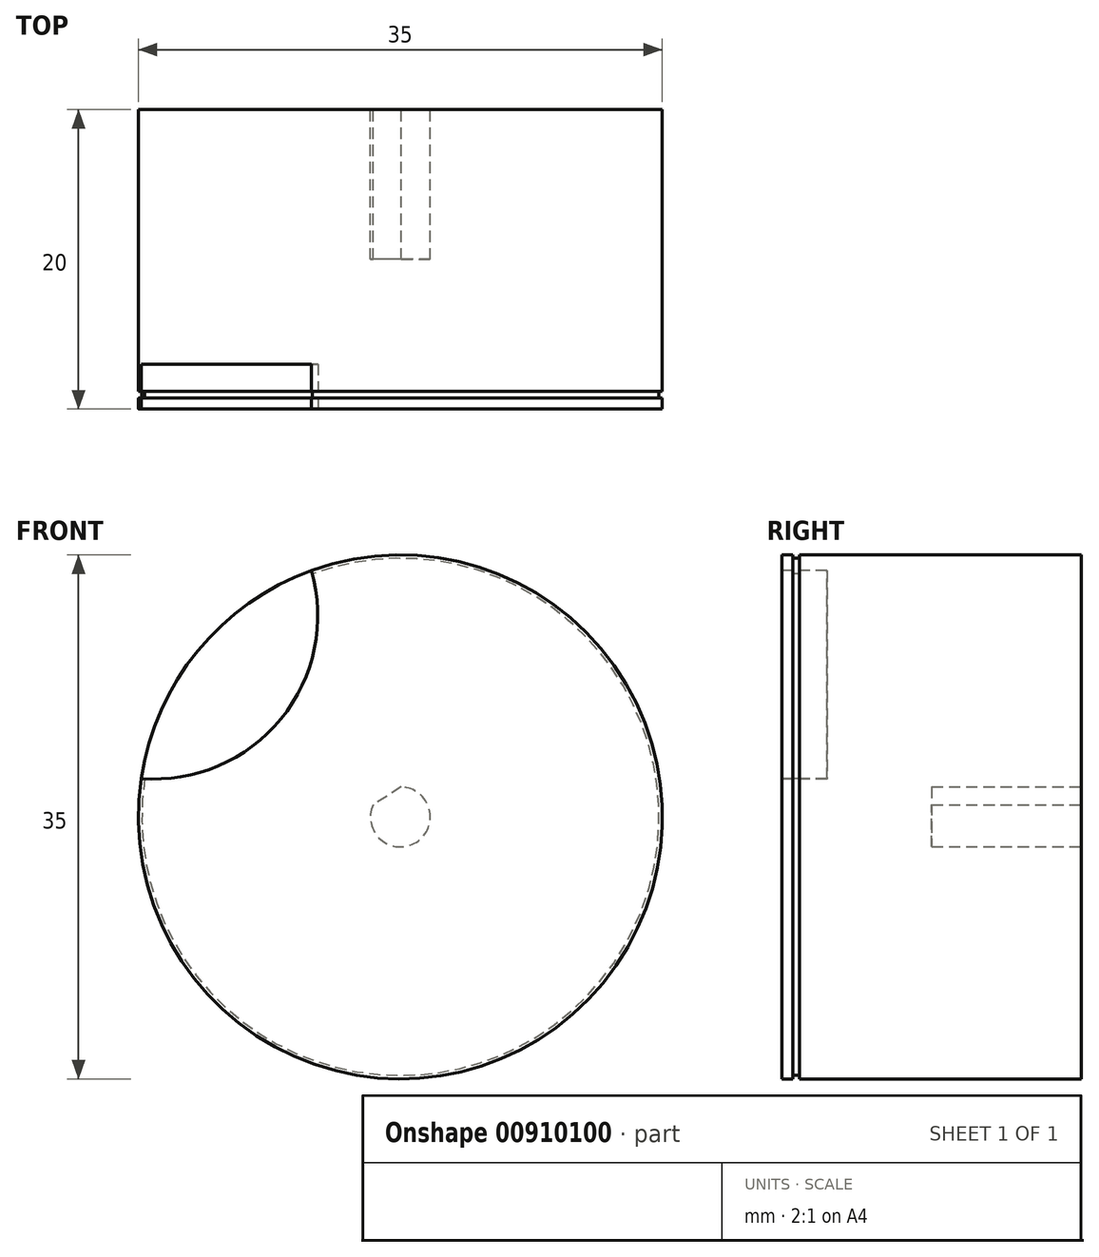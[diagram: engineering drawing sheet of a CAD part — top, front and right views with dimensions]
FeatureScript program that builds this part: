
annotation { "Feature Type Name" : "Feature", "Feature Type Description" : "" }
export const myFeature = defineFeature(function(context is Context, id is Id, definition is map)
    precondition{}
    {
        {
            var Q0;
            Q0=qCreatedBy(makeId("Front.planeOp"),FACE);
            var sketch = newSketch(context, id + "F0", { "sketchPlane" : qUnion([Q0])});
            skCircle(sketch, "E0", {"center": v(0, 0) * mm, "radius": 17.5 * mm});
            skSolve(sketch);
        }
        {
            var Q0;
            Q0 = qSketchRegion(id + "F0", true);
            extrude(context, id + "F1", {"entities" : qUnion([Q0]), "oppositeDirection" : true, "depth" : 20 * mm, "offsetDistance" : 25 * mm});
        }
        {
            var Q0;
            Q0=qCreatedBy(makeId("Front.planeOp"),FACE);
            var sketch = newSketch(context, id + "F2", { "sketchPlane" : qUnion([Q0])});
            skCircle(sketch, "E1", {"center": v(-16.44, 13.46) * mm, "radius": 10.93 * mm});
            skSolve(sketch);
        }
        {
            var Q0;
            Q0=makeQuery(id+"F2.imprint","IMPRINT",FACE,{"disambiguationData":[TD([[makeQuery(id+"F2.imprint","IMPRINT",EDGE,{"derivedFrom":sQuery(id+"F2.wireOp",EDGE,"E1")}),1.0]])]});
            extrude(context, id + "F3", {"entities" : qUnion([Q0]), "operationType" : NewBodyOperationType.REMOVE, "oppositeDirection" : true, "depth" : 3 * mm, "offsetDistance" : 25 * mm});
        }
        {
            var Q0;
            Q0=makeQuery(id+"F1.opExtrude","CAP_FACE",FACE,{"disambiguationData":[OSD([sQuery(id+"F0.wireOp",EDGE,"E0")])],"isStart":false});
            var sketch = newSketch(context, id + "F4", { "sketchPlane" : qUnion([Q0])});
            skCircle(sketch, "E2", {"center": v(0, 0) * mm, "radius": 2 * mm});
            skLineSegment(sketch, "E3", {"start": v(-0.07, 2) * mm, "end": v(1.83, 0.8) * mm});
            skSolve(sketch);
        }
        {
            var Q0;
            {var subQ0=sQuery(id+"F4.wireOp",EDGE,"E3");Q0=makeQuery(id+"F4.imprint","IMPRINT",FACE,{"disambiguationData":[TD([[makeQuery(id+"F4.imprint","IMPRINT",EDGE,{"derivedFrom":subQ0}),-1.0]])]});}
            extrude(context, id + "F5", {"entities" : qUnion([Q0]), "operationType" : NewBodyOperationType.REMOVE, "oppositeDirection" : true, "depth" : 10 * mm, "offsetDistance" : 25 * mm});
        }
        {
            var Q0;
            Q0=qCreatedBy(makeId("Right.planeOp"),FACE);
            var sketch = newSketch(context, id + "F6", { "sketchPlane" : qUnion([Q0])});
            skLineSegment(sketch, "E4.bottom", {"start": v(0.73, 17.53) * mm, "end": v(1.18, 17.53) * mm});
            skLineSegment(sketch, "E4.top", {"start": v(0.73, 17.27) * mm, "end": v(1.18, 17.27) * mm});
            skLineSegment(sketch, "E4.left", {"start": v(0.73, 17.53) * mm, "end": v(0.73, 17.27) * mm});
            skLineSegment(sketch, "E4.right", {"start": v(1.18, 17.53) * mm, "end": v(1.18, 17.27) * mm});
            skSolve(sketch);
        }
        {
            var Q0;
            Q0 = qSketchRegion(id + "F6", true);
            var Q1;
            Q1=makeQuery(id+"F1.opExtrude","SWEPT_FACE",FACE,{"disambiguationData":[OSD([sQuery(id+"F0.wireOp",EDGE,"E0")])]});
            revolve(context, id + "F7", {"operationType" : NewBodyOperationType.REMOVE, "surfaceOperationType" : NewSurfaceOperationType.NEW, "entities" : qUnion([Q0]), "axis" : qUnion([Q1]), "revolveType" : RevolveType.ONE_DIRECTION, "oppositeDirection" : true, "angle" : 360 * degree});
        }
    });
